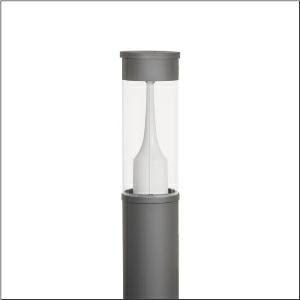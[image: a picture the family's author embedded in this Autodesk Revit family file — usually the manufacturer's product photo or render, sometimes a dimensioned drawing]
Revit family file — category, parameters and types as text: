
# Revit family: city-light_260_iq___st1_2a_5xa5295af14h_a960
name_source: partatom
category: Lighting Fixtures
units: mm (PartAtom-declared; Revit-internal decimal feet)

## family parameters
Cut with Voids When Loaded = No
Host = Face
Light Source = No
Part Type = Normal
Room Calculation Point = No
Round Connector Dimension = Use Diameter
Shared = No

## types (1)
- --- (1 x LED, 1540 lm, 12.9 W, 2200K)
    Apparent Load = 13 VA
    CIE Flux Codes = 22 61 93 96 100
    Color Rendering = 70
    Color Temperature = 2200K
    Default Elevation = 1800 mm
    Description = City-Light 260 iQ, light pillar, Module 540 iQ-SR, primary light control with 3 zone facetted reflector, of plastic, silver coated, highly specular, structured, primary optical cover: cover, of PMMA, transparent, partly coated, light distribution: ST1.2a, primary light characteristic: asymmetric, LED, High Power LED, rated luminous flux: 1.540lm, luminous efficacy: 119lm/W, light colour: 722, colour temperature: 2200K, control gear: iQ Street-Remote, control: pre-setting: logarithmic dimming characteristic, Street-Remote, Auto-Match, Temp-Guard, Lumen-Switch, Night-Set, Smart-Wire, Light-Fading, Desk-Remote (wireless, voltage-free reading and setting of iQ features in the workshop via application-optimized NFC function/RFID function), optimised constant luminous flux control (CLO 2.0), with terminal, 6-pole, max. 2.5mm², mains connection: 230..240V, AC, 50/60Hz, start of lifetime: 13W, end of service life: 13W, reduction: 6W, luminaire housing, cylindrical, of extruded aluminium section, coated, Siteco® metallic grey (DB 702S), length: 2.600mm, diameter: 200mm, Module 540 iQ-SR, traffic white (RAL 9016), equipment: standard, protection rating (complete): IP65, insulation class (complete): insulation class II (safety insulation), certification: CE, ENEC, VDE, packaging unit: 1 piece

Light Distribution: ST1.2a
    Height = 500 mm
    Lamp = 1 x LED
    Lamp Light Flux = 1540 lm
    Lamp Power = 12.9 W
    Lamp count = 1
    Length = 200 mm  [stored 0.656168 ft]
    Luminous efficacy = 119 lm/W
    Manufacturer = Siteco
    ModVariant = No
    Model = 5XA5295AF14H
    Mounting Place = Floor
    Mounting Type = Freestanding
    Number of Poles = 1
    OnlyDefault = Yes
    Power Factor = 1
    Product Name = City-Light 260 iQ | ST1.2a
    Product group = light pillar
    ProductGroupID = 1301
    Protection Class = Protection class II
    Protection Degree = IP 65
    RLX_Detail_Level = 1
    RLX_Emergency_Light_Flux = 0 lm
    RLX_Emergency_Type = 0
    RLX_Emergency_Type_DB = No
    RlxData = <blob elided: 61105 chars, md5=0a229a30>
    Socket = socket
    Standby Power = 0 W
    System Light Flux = 1540 lm
    System Power = 13 W
    Type Comments = factory setting: luminous flux: 100 % | dim-lin: 254 | 516 mA
    Type Image = l_1006918.jpg
    URL = http://relux.com
    VarID = @adj_160269
    Voltage = 0 V
    Weight = 0.00 kg
    Width = 0 mm  [stored 0 ft]

note: [stored X ft] marks values corroborated as IEEE doubles in the binary element streams (Revit-internal decimal feet)

## geometry (parser evidence)
native form markers: Blend x4, Sweep x12
no freeform markers — native parametric forms only
